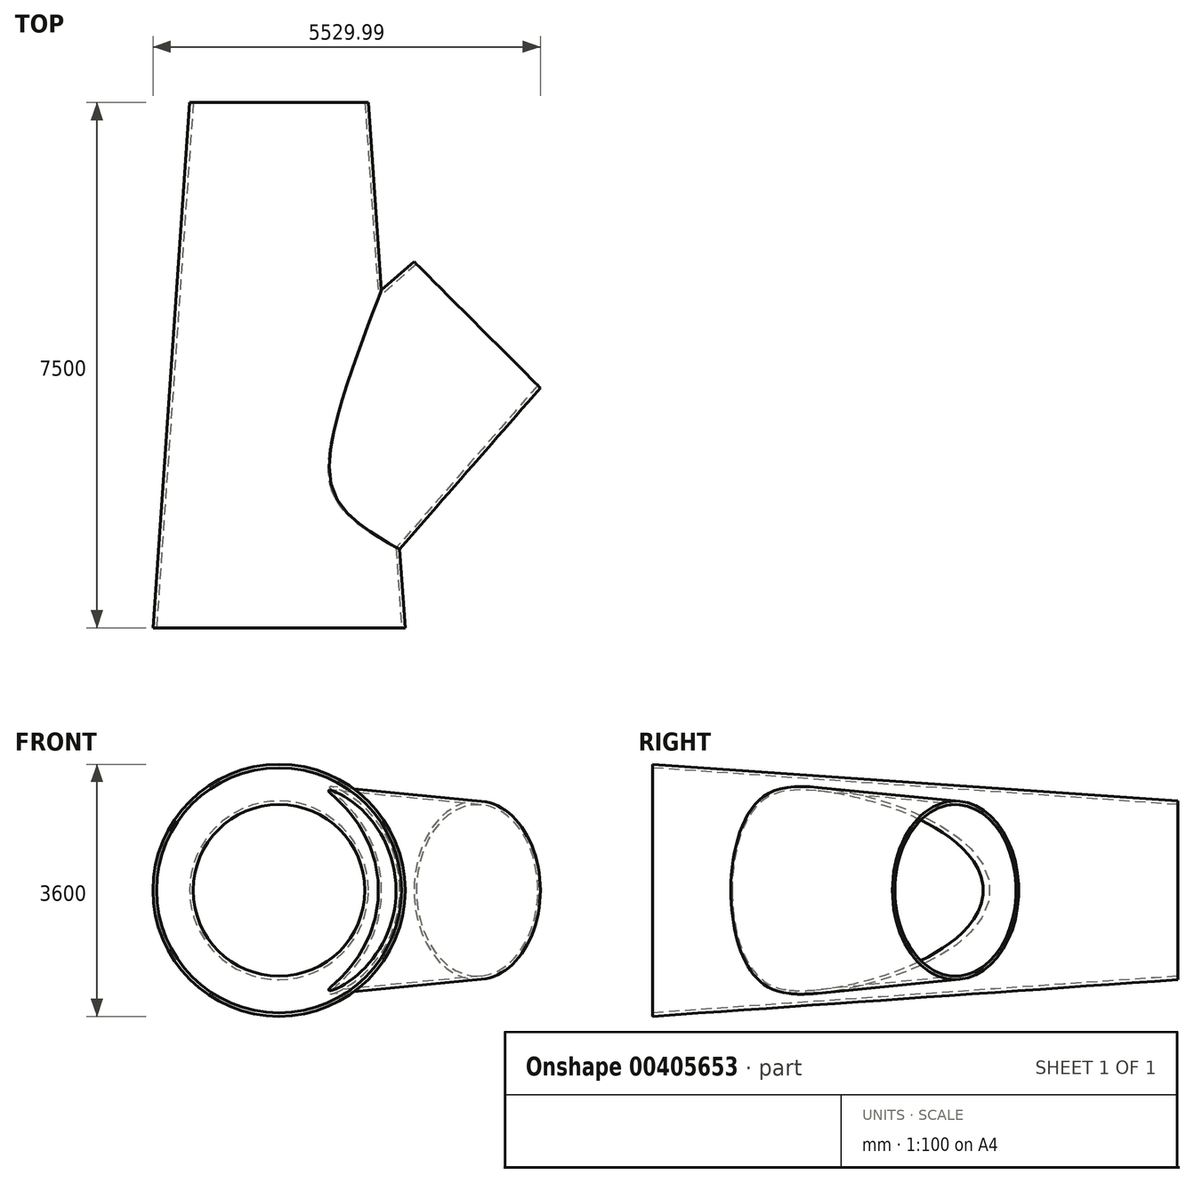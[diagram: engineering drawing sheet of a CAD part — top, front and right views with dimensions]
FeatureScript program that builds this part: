
annotation { "Feature Type Name" : "Feature", "Feature Type Description" : "" }
export const myFeature = defineFeature(function(context is Context, id is Id, definition is map)
    precondition{}
    {
        {
            var Q0;
            Q0=qCreatedBy(makeId("Right.planeOp"),FACE);
            var sketch = newSketch(context, id + "F0", { "sketchPlane" : qUnion([Q0])});
            skLineSegment(sketch, "E0", {"start": v(0, 0) * mm, "end": v(7500, 0) * mm});
            skSolve(sketch);
        }
        {
            var Q0;
            Q0=qCreatedBy(makeId("Top.planeOp"),FACE);
            var sketch = newSketch(context, id + "F1", { "sketchPlane" : qUnion([Q0])});
            skLineSegment(sketch, "E1", {"start": v(0, 1500) * mm, "end": v(2828.43, 4328.43) * mm});
            skLineSegment(sketch, "E2", {"start": v(0, 1500) * mm, "end": v(1060.66, 439.34) * mm});
            skLineSegment(sketch, "E3", {"start": v(2828.43, 4328.43) * mm, "end": v(3694.63, 3462.22) * mm});
            skLineSegment(sketch, "E4", {"start": v(1060.66, 439.34) * mm, "end": v(3694.63, 3462.22) * mm});
            skLineSegment(sketch, "E5", {"start": v(1060.66, 439.34) * mm, "end": v(1096.02, 403.98) * mm});
            skLineSegment(sketch, "E6", {"start": v(3694.63, 3462.22) * mm, "end": v(3729.99, 3426.87) * mm});
            skLineSegment(sketch, "E7", {"start": v(3729.99, 3426.87) * mm, "end": v(1096.02, 403.98) * mm});
            skSolve(sketch);
        }
        {
            var Q0;
            Q0=qCreatedBy(makeId("Top.planeOp"),FACE);
            var sketch = newSketch(context, id + "F2", { "sketchPlane" : qUnion([Q0])});
            skLineSegment(sketch, "E8", {"start": v(0, 0) * mm, "end": v(-1750, 0) * mm});
            skLineSegment(sketch, "E9", {"start": v(0, 7500) * mm, "end": v(-1225, 7500) * mm});
            skLineSegment(sketch, "E10", {"start": v(-1750, 0) * mm, "end": v(-1225, 7500) * mm});
            skLineSegment(sketch, "E11", {"start": v(-1225, 7500) * mm, "end": v(-1275, 7500) * mm});
            skLineSegment(sketch, "E12", {"start": v(-1750, 0) * mm, "end": v(-1800, 0) * mm});
            skLineSegment(sketch, "E13", {"start": v(-1800, 0) * mm, "end": v(-1275, 7500) * mm});
            skLineSegment(sketch, "E14", {"start": v(0, 7500) * mm, "end": v(0, 0) * mm});
            skSolve(sketch);
        }
        {
            var Q0;
            Q0=makeQuery(id+"F2.imprint","IMPRINT",FACE,{"disambiguationData":[TD([[makeQuery(id+"F2.imprint","IMPRINT",EDGE,{"derivedFrom":sQuery(id+"F2.wireOp",EDGE,"E10")}),1.0]])]});
            var Q1;
            Q1=sQuery(id+"F0.wireOp",EDGE,"E0");
            revolve(context, id + "F3", {"entities" : qUnion([Q0]), "axis" : qUnion([Q1]), "revolveType" : RevolveType.FULL});
        }
        {
            var Q0;
            Q0=makeQuery(id+"F1.imprint","IMPRINT",FACE,{"disambiguationData":[TD([[makeQuery(id+"F1.imprint","IMPRINT",EDGE,{"derivedFrom":sQuery(id+"F1.wireOp",EDGE,"E4")}),-1.0]])]});
            var Q1;
            Q1=sQuery(id+"F1.wireOp",EDGE,"E1");
            revolve(context, id + "F4", {"operationType" : NewBodyOperationType.ADD, "entities" : qUnion([Q0]), "axis" : qUnion([Q1]), "revolveType" : RevolveType.FULL});
        }
        {
            var Q0;
            Q0=makeQuery(id+"F1.imprint","IMPRINT",FACE,{"disambiguationData":[TD([[makeQuery(id+"F1.imprint","IMPRINT",EDGE,{"derivedFrom":sQuery(id+"F1.wireOp",EDGE,"E1")}),-1.0]])]});
            var Q1;
            Q1=sQuery(id+"F1.wireOp",EDGE,"E1");
            revolve(context, id + "F5", {"operationType" : NewBodyOperationType.REMOVE, "entities" : qUnion([Q0]), "axis" : qUnion([Q1]), "revolveType" : RevolveType.FULL, "oppositeDirection" : true});
        }
        {
            var Q0;
            Q0=makeQuery(id+"F2.imprint","IMPRINT",FACE,{"disambiguationData":[TD([[makeQuery(id+"F2.imprint","IMPRINT",EDGE,{"derivedFrom":sQuery(id+"F2.wireOp",EDGE,"E8")}),-1.0]])]});
            var Q1;
            Q1=sQuery(id+"F0.wireOp",EDGE,"E0");
            revolve(context, id + "F6", {"operationType" : NewBodyOperationType.REMOVE, "entities" : qUnion([Q0]), "axis" : qUnion([Q1]), "revolveType" : RevolveType.FULL, "oppositeDirection" : true});
        }
    });
